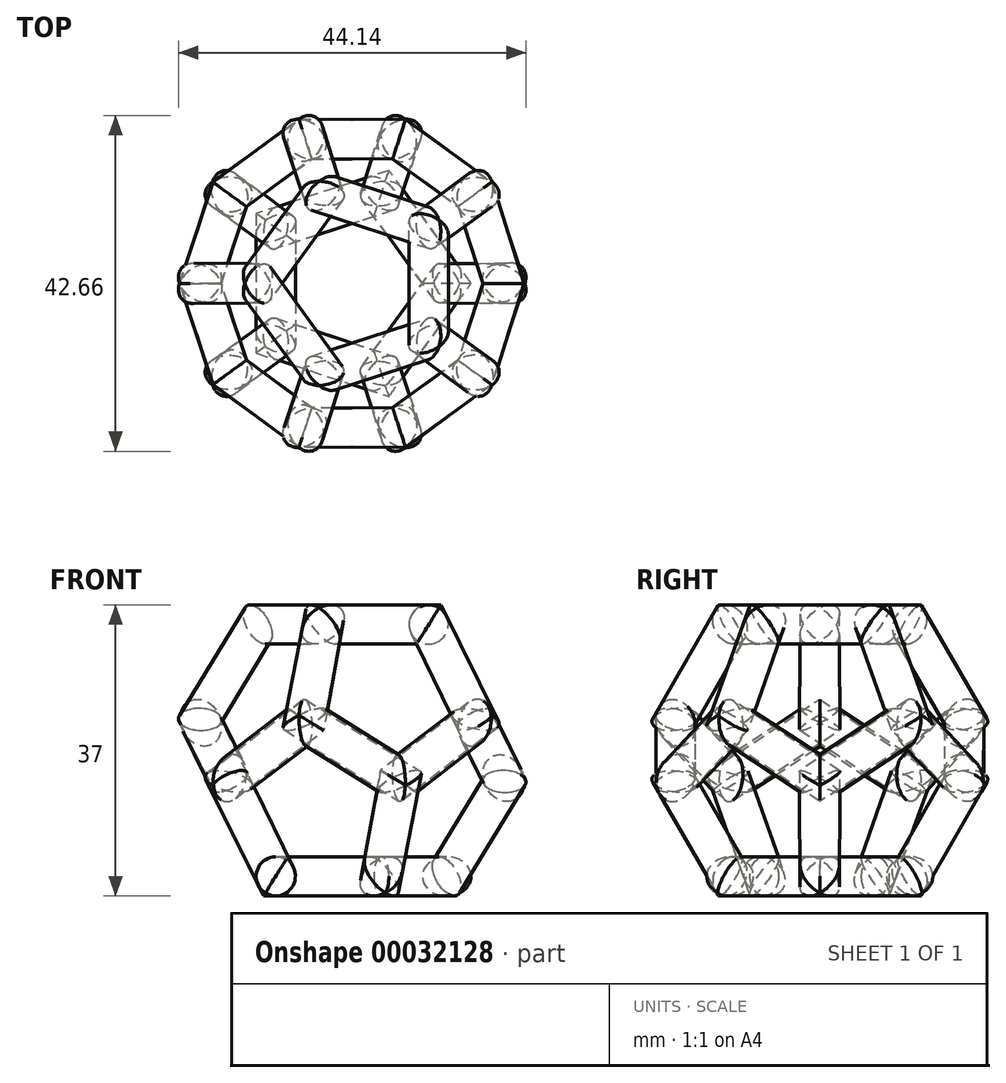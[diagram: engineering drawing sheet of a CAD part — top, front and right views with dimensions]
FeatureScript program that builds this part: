
annotation { "Feature Type Name" : "Feature", "Feature Type Description" : "" }
export const myFeature = defineFeature(function(context is Context, id is Id, definition is map)
    precondition{}
    {
        {
            var Q0;
            Q0=qCreatedBy(makeId("Top.planeOp"),FACE);
            var sketch = newSketch(context, id + "F0", { "sketchPlane" : qUnion([Q0])});
            skLineSegment(sketch, "E0", {"start": v(0, 0) * mm, "end": v(12, 0) * mm});
            skLineSegment(sketch, "E1", {"start": v(12, 0) * mm, "end": v(3.7, 11.41) * mm});
            skLineSegment(sketch, "E2", {"start": v(3.7, 11.41) * mm, "end": v(0, 0) * mm});
            skLineSegment(sketch, "E3.1.0", {"start": v(3.7, 11.41) * mm, "end": v(-9.7, 7.05) * mm});
            skLineSegment(sketch, "E3.2.0", {"start": v(-9.7, 7.05) * mm, "end": v(-9.7, -7.05) * mm});
            skLineSegment(sketch, "E3.3.0", {"start": v(-9.7, -7.05) * mm, "end": v(3.7, -11.41) * mm});
            skLineSegment(sketch, "E3.4.0", {"start": v(3.7, -11.41) * mm, "end": v(12, 0) * mm});
            skPoint(sketch, "E3.center", {"position": v(0, 0) * mm});
            skSolve(sketch);
        }
        {
            var Q0;
            Q0=qCreatedBy(makeId("Front.planeOp"),FACE);
            var sketch = newSketch(context, id + "F1", { "sketchPlane" : qUnion([Q0])});
            skLineSegment(sketch, "E4.1", {"start": v(-9.7, 0) * mm, "end": v(3.7, 0) * mm});
            skCircle(sketch, "E5", {"center": v(-9.7, 0) * mm, "radius": 2.5 * mm});
            skSolve(sketch);
        }
        {
            var Q0;
            Q0=makeQuery(id+"F1.imprint","IMPRINT",FACE,{"disambiguationData":[TD([[makeQuery(id+"F1.imprint","IMPRINT",EDGE,{"derivedFrom":sQuery(id+"F1.wireOp",EDGE,"E5")}),1.0]])]});
            var Q1;
            Q1=sQuery(id+"F0.wireOp",EDGE,"E3.2.0");
            var Q2;
            Q2=sQuery(id+"F0.wireOp",EDGE,"E3.3.0");
            var Q3;
            Q3=sQuery(id+"F0.wireOp",EDGE,"E3.4.0");
            var Q4;
            Q4=sQuery(id+"F0.wireOp",EDGE,"E1");
            var Q5;
            Q5=sQuery(id+"F0.wireOp",EDGE,"E3.1.0");
            sweep(context, id + "F2", {"profiles" : qUnion([Q0]), "path" : qUnion([Q1, Q2, Q3, Q4, Q5])});
        }
        {
            var Q0;
            Q0=makeQuery(id+"F2.opSweep","SWEPT_BODY",BODY,{"disambiguationData":[OSD([sQuery(id+"F0.wireOp",EDGE,"E3.1.0"),sQuery(id+"F1.wireOp",EDGE,"E5")])]});
            var Q1;
            Q1=sQuery(id+"F0.wireOp",EDGE,"E3.1.0");
            transform(context, id + "F3", {"entities" : qUnion([Q0]), "transformType" : TransformType.ROTATION, "transformAxis" : qUnion([Q1]), "angle" : 116 * degree, "makeCopy" : true});
        }
        {
            var Q0;
            Q0=qCreatedBy(makeId("Right.planeOp"),FACE);
            var sketch = newSketch(context, id + "F4", { "sketchPlane" : qUnion([Q0])});
            skLineSegment(sketch, "E6", {"start": v(0, 0) * mm, "end": v(0, 32) * mm});
            skSolve(sketch);
        }
        {
            var Q0;
            Q0=makeQuery(id+"F3.opPattern","COPY",BODY,{"derivedFrom":makeQuery(id+"F2.opSweep","SWEPT_BODY",BODY,{"disambiguationData":[OSD([sQuery(id+"F0.wireOp",EDGE,"E3.1.0"),sQuery(id+"F1.wireOp",EDGE,"E5")])]}),"instanceName":"1"});
            var Q1;
            Q1=sQuery(id+"F4.wireOp",EDGE,"E6");
            circularPattern(context, id + "F5", {"entities" : qUnion([Q0]), "axis" : qUnion([Q1]), "angle" : 360 * degree, "instanceCount" : 5, "equalSpace" : true});
        }
        {
            var Q0;
            Q0=makeQuery(id+"F2.opSweep","SWEPT_BODY",BODY,{"disambiguationData":[OSD([sQuery(id+"F0.wireOp",EDGE,"E3.1.0"),sQuery(id+"F1.wireOp",EDGE,"E5")])]});
            var Q1;
            Q1=makeQuery(id+"F3.opPattern","COPY",BODY,{"derivedFrom":makeQuery(id+"F2.opSweep","SWEPT_BODY",BODY,{"disambiguationData":[OSD([sQuery(id+"F0.wireOp",EDGE,"E3.1.0"),sQuery(id+"F1.wireOp",EDGE,"E5")])]}),"instanceName":"1"});
            var Q2;
            Q2=makeQuery(id+"F5.opPattern","COPY",BODY,{"derivedFrom":makeQuery(id+"F3.opPattern","COPY",BODY,{"derivedFrom":makeQuery(id+"F2.opSweep","SWEPT_BODY",BODY,{"disambiguationData":[OSD([sQuery(id+"F0.wireOp",EDGE,"E3.1.0"),sQuery(id+"F1.wireOp",EDGE,"E5")])]}),"instanceName":"1"}),"instanceName":"2"});
            var Q3;
            Q3=makeQuery(id+"F5.opPattern","COPY",BODY,{"derivedFrom":makeQuery(id+"F3.opPattern","COPY",BODY,{"derivedFrom":makeQuery(id+"F2.opSweep","SWEPT_BODY",BODY,{"disambiguationData":[OSD([sQuery(id+"F0.wireOp",EDGE,"E3.1.0"),sQuery(id+"F1.wireOp",EDGE,"E5")])]}),"instanceName":"1"}),"instanceName":"4"});
            var Q4;
            Q4=makeQuery(id+"F5.opPattern","COPY",BODY,{"derivedFrom":makeQuery(id+"F3.opPattern","COPY",BODY,{"derivedFrom":makeQuery(id+"F2.opSweep","SWEPT_BODY",BODY,{"disambiguationData":[OSD([sQuery(id+"F0.wireOp",EDGE,"E3.1.0"),sQuery(id+"F1.wireOp",EDGE,"E5")])]}),"instanceName":"1"}),"instanceName":"3"});
            var Q5;
            Q5=makeQuery(id+"F5.opPattern","COPY",BODY,{"derivedFrom":makeQuery(id+"F3.opPattern","COPY",BODY,{"derivedFrom":makeQuery(id+"F2.opSweep","SWEPT_BODY",BODY,{"disambiguationData":[OSD([sQuery(id+"F0.wireOp",EDGE,"E3.1.0"),sQuery(id+"F1.wireOp",EDGE,"E5")])]}),"instanceName":"1"}),"instanceName":"1"});
            var Q6;
            Q6=qCreatedBy(makeId("Top.planeOp"),FACE);
            mirror(context, id + "F6", {"entities" : qUnion([Q0, Q1, Q2, Q3, Q4, Q5]), "mirrorPlane" : qUnion([Q6])});
        }
        {
            var Q0;
            Q0=makeQuery(id+"F6.opPattern","COPY",BODY,{"derivedFrom":makeQuery(id+"F5.opPattern","COPY",BODY,{"derivedFrom":makeQuery(id+"F3.opPattern","COPY",BODY,{"derivedFrom":makeQuery(id+"F2.opSweep","SWEPT_BODY",BODY,{"disambiguationData":[OSD([sQuery(id+"F0.wireOp",EDGE,"E3.1.0"),sQuery(id+"F1.wireOp",EDGE,"E5")])]}),"instanceName":"1"}),"instanceName":"4"}),"instanceName":"1"});
            var Q1;
            Q1=makeQuery(id+"F6.opPattern","COPY",BODY,{"derivedFrom":makeQuery(id+"F5.opPattern","COPY",BODY,{"derivedFrom":makeQuery(id+"F3.opPattern","COPY",BODY,{"derivedFrom":makeQuery(id+"F2.opSweep","SWEPT_BODY",BODY,{"disambiguationData":[OSD([sQuery(id+"F0.wireOp",EDGE,"E3.1.0"),sQuery(id+"F1.wireOp",EDGE,"E5")])]}),"instanceName":"1"}),"instanceName":"3"}),"instanceName":"1"});
            var Q2;
            Q2=makeQuery(id+"F6.opPattern","COPY",BODY,{"derivedFrom":makeQuery(id+"F5.opPattern","COPY",BODY,{"derivedFrom":makeQuery(id+"F3.opPattern","COPY",BODY,{"derivedFrom":makeQuery(id+"F2.opSweep","SWEPT_BODY",BODY,{"disambiguationData":[OSD([sQuery(id+"F0.wireOp",EDGE,"E3.1.0"),sQuery(id+"F1.wireOp",EDGE,"E5")])]}),"instanceName":"1"}),"instanceName":"2"}),"instanceName":"1"});
            var Q3;
            Q3=makeQuery(id+"F6.opPattern","COPY",BODY,{"derivedFrom":makeQuery(id+"F5.opPattern","COPY",BODY,{"derivedFrom":makeQuery(id+"F3.opPattern","COPY",BODY,{"derivedFrom":makeQuery(id+"F2.opSweep","SWEPT_BODY",BODY,{"disambiguationData":[OSD([sQuery(id+"F0.wireOp",EDGE,"E3.1.0"),sQuery(id+"F1.wireOp",EDGE,"E5")])]}),"instanceName":"1"}),"instanceName":"1"}),"instanceName":"1"});
            var Q4;
            Q4=makeQuery(id+"F6.opPattern","COPY",BODY,{"derivedFrom":makeQuery(id+"F3.opPattern","COPY",BODY,{"derivedFrom":makeQuery(id+"F2.opSweep","SWEPT_BODY",BODY,{"disambiguationData":[OSD([sQuery(id+"F0.wireOp",EDGE,"E3.1.0"),sQuery(id+"F1.wireOp",EDGE,"E5")])]}),"instanceName":"1"}),"instanceName":"1"});
            var Q5;
            Q5=sQuery(id+"F4.wireOp",EDGE,"E6");
            transform(context, id + "F7", {"entities" : qUnion([Q0, Q1, Q2, Q3, Q4]), "transformType" : TransformType.ROTATION, "transformAxis" : qUnion([Q5]), "angle" : 36 * degree, "makeCopy" : false});
        }
        {
            var Q0;
            Q0=makeQuery(id+"F6.opPattern","COPY",BODY,{"derivedFrom":makeQuery(id+"F5.opPattern","COPY",BODY,{"derivedFrom":makeQuery(id+"F3.opPattern","COPY",BODY,{"derivedFrom":makeQuery(id+"F2.opSweep","SWEPT_BODY",BODY,{"disambiguationData":[OSD([sQuery(id+"F0.wireOp",EDGE,"E3.1.0"),sQuery(id+"F1.wireOp",EDGE,"E5")])]}),"instanceName":"1"}),"instanceName":"4"}),"instanceName":"1"});
            var Q1;
            Q1=makeQuery(id+"F6.opPattern","COPY",BODY,{"derivedFrom":makeQuery(id+"F5.opPattern","COPY",BODY,{"derivedFrom":makeQuery(id+"F3.opPattern","COPY",BODY,{"derivedFrom":makeQuery(id+"F2.opSweep","SWEPT_BODY",BODY,{"disambiguationData":[OSD([sQuery(id+"F0.wireOp",EDGE,"E3.1.0"),sQuery(id+"F1.wireOp",EDGE,"E5")])]}),"instanceName":"1"}),"instanceName":"3"}),"instanceName":"1"});
            var Q2;
            Q2=makeQuery(id+"F6.opPattern","COPY",BODY,{"derivedFrom":makeQuery(id+"F5.opPattern","COPY",BODY,{"derivedFrom":makeQuery(id+"F3.opPattern","COPY",BODY,{"derivedFrom":makeQuery(id+"F2.opSweep","SWEPT_BODY",BODY,{"disambiguationData":[OSD([sQuery(id+"F0.wireOp",EDGE,"E3.1.0"),sQuery(id+"F1.wireOp",EDGE,"E5")])]}),"instanceName":"1"}),"instanceName":"2"}),"instanceName":"1"});
            var Q3;
            Q3=makeQuery(id+"F6.opPattern","COPY",BODY,{"derivedFrom":makeQuery(id+"F5.opPattern","COPY",BODY,{"derivedFrom":makeQuery(id+"F3.opPattern","COPY",BODY,{"derivedFrom":makeQuery(id+"F2.opSweep","SWEPT_BODY",BODY,{"disambiguationData":[OSD([sQuery(id+"F0.wireOp",EDGE,"E3.1.0"),sQuery(id+"F1.wireOp",EDGE,"E5")])]}),"instanceName":"1"}),"instanceName":"1"}),"instanceName":"1"});
            var Q4;
            Q4=makeQuery(id+"F6.opPattern","COPY",BODY,{"derivedFrom":makeQuery(id+"F3.opPattern","COPY",BODY,{"derivedFrom":makeQuery(id+"F2.opSweep","SWEPT_BODY",BODY,{"disambiguationData":[OSD([sQuery(id+"F0.wireOp",EDGE,"E3.1.0"),sQuery(id+"F1.wireOp",EDGE,"E5")])]}),"instanceName":"1"}),"instanceName":"1"});
            var Q5;
            Q5=sQuery(id+"F4.wireOp",EDGE,"E6");
            transform(context, id + "F8", {"entities" : qUnion([Q0, Q1, Q2, Q3, Q4]), "transformType" : TransformType.TRANSLATION_ENTITY, "oppositeDirectionEntity" : false, "transformLine" : qUnion([Q5]), "makeCopy" : false});
        }
    });
